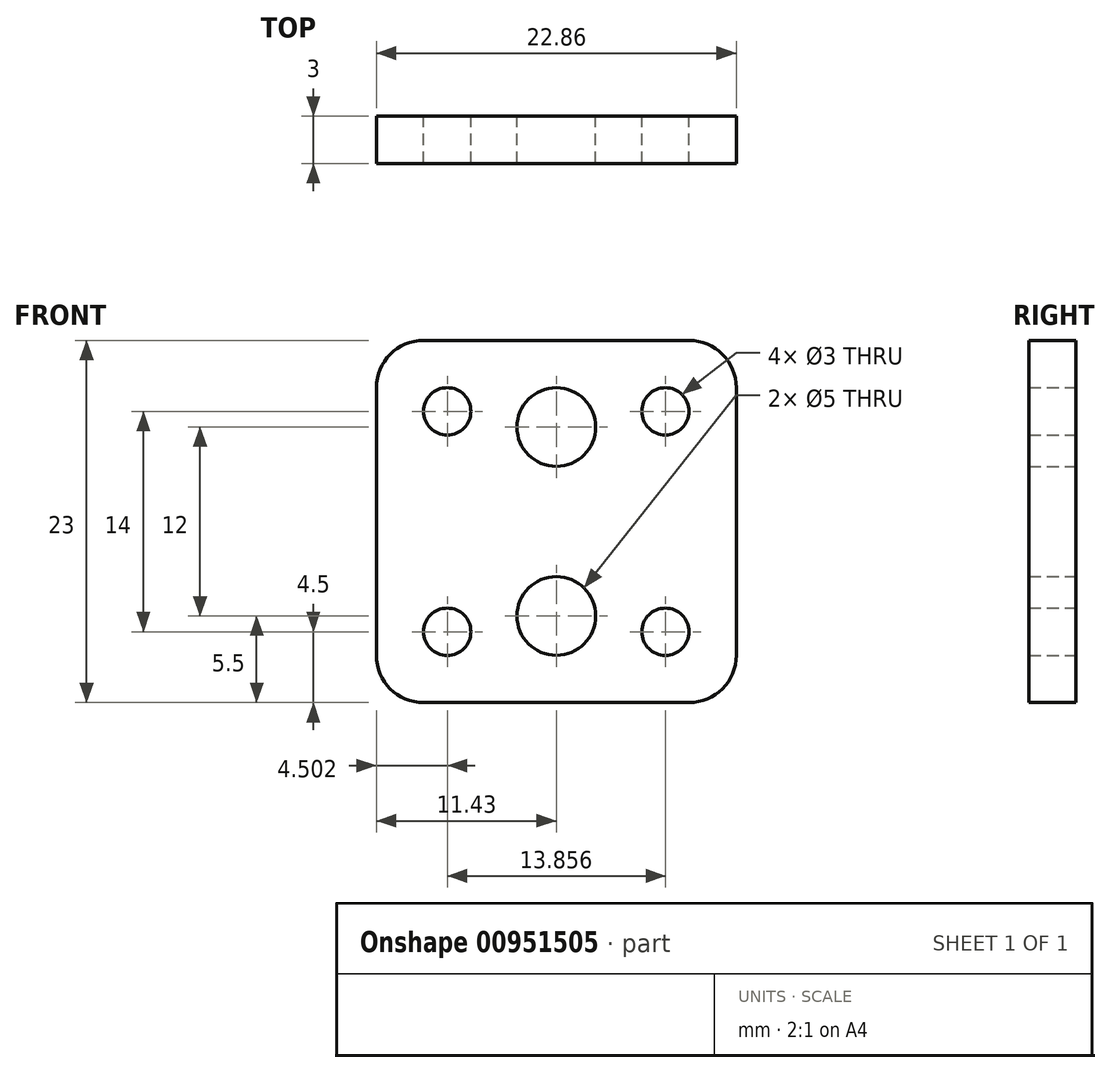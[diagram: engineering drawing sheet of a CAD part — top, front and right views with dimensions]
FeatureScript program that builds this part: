
annotation { "Feature Type Name" : "Feature", "Feature Type Description" : "" }
export const myFeature = defineFeature(function(context is Context, id is Id, definition is map)
    precondition{}
    {
        {
            var Q0;
            Q0=qCreatedBy(makeId("Front.planeOp"),FACE);
            var sketch = newSketch(context, id + "F0", { "sketchPlane" : qUnion([Q0])});
            skLineSegment(sketch, "E0.bottom", {"start": v(-8.43, -11.5) * mm, "end": v(8.43, -11.5) * mm});
            skLineSegment(sketch, "E0.top", {"start": v(-8.43, 11.5) * mm, "end": v(8.43, 11.5) * mm});
            skLineSegment(sketch, "E0.left", {"start": v(-11.43, -8.5) * mm, "end": v(-11.43, 8.5) * mm});
            skLineSegment(sketch, "E0.right", {"start": v(11.43, -8.5) * mm, "end": v(11.43, 8.5) * mm});
            skCircle(sketch, "E1", {"center": v(0, 6) * mm, "radius": 2.5 * mm});
            skCircle(sketch, "E2", {"center": v(0, -6) * mm, "radius": 2.5 * mm});
            skCircle(sketch, "E3", {"center": v(6.93, 7) * mm, "radius": 1.5 * mm});
            skCircle(sketch, "E4", {"center": v(-6.93, 7) * mm, "radius": 1.5 * mm});
            skCircle(sketch, "E5", {"center": v(-6.93, -7) * mm, "radius": 1.5 * mm});
            skCircle(sketch, "E6", {"center": v(6.93, -7) * mm, "radius": 1.5 * mm});
            skPoint(sketch, "E7.visualSharp", {"position": v(11.43, 11.5) * mm});
            skArc(sketch, "E7.filletArc", {"start": v(11.43, 8.5) * mm, "mid": v(10.55, 10.62) * mm, "end": v(8.43, 11.5) * mm});
            skPoint(sketch, "E8.visualSharp", {"position": v(-11.43, 11.5) * mm});
            skArc(sketch, "E8.filletArc", {"start": v(-8.43, 11.5) * mm, "mid": v(-10.55, 10.62) * mm, "end": v(-11.43, 8.5) * mm});
            skPoint(sketch, "E9.visualSharp", {"position": v(-11.43, -11.5) * mm});
            skArc(sketch, "E9.filletArc", {"start": v(-11.43, -8.5) * mm, "mid": v(-10.55, -10.62) * mm, "end": v(-8.43, -11.5) * mm});
            skPoint(sketch, "E10.visualSharp", {"position": v(11.43, -11.5) * mm});
            skArc(sketch, "E10.filletArc", {"start": v(8.43, -11.5) * mm, "mid": v(10.55, -10.62) * mm, "end": v(11.43, -8.5) * mm});
            skSolve(sketch);
        }
        {
            var Q0;
            Q0 = qSketchRegion(id + "F0", true);
            extrude(context, id + "F1", {"entities" : qUnion([Q0]), "depth" : 3 * mm, "offsetDistance" : 25 * mm});
        }
    });
